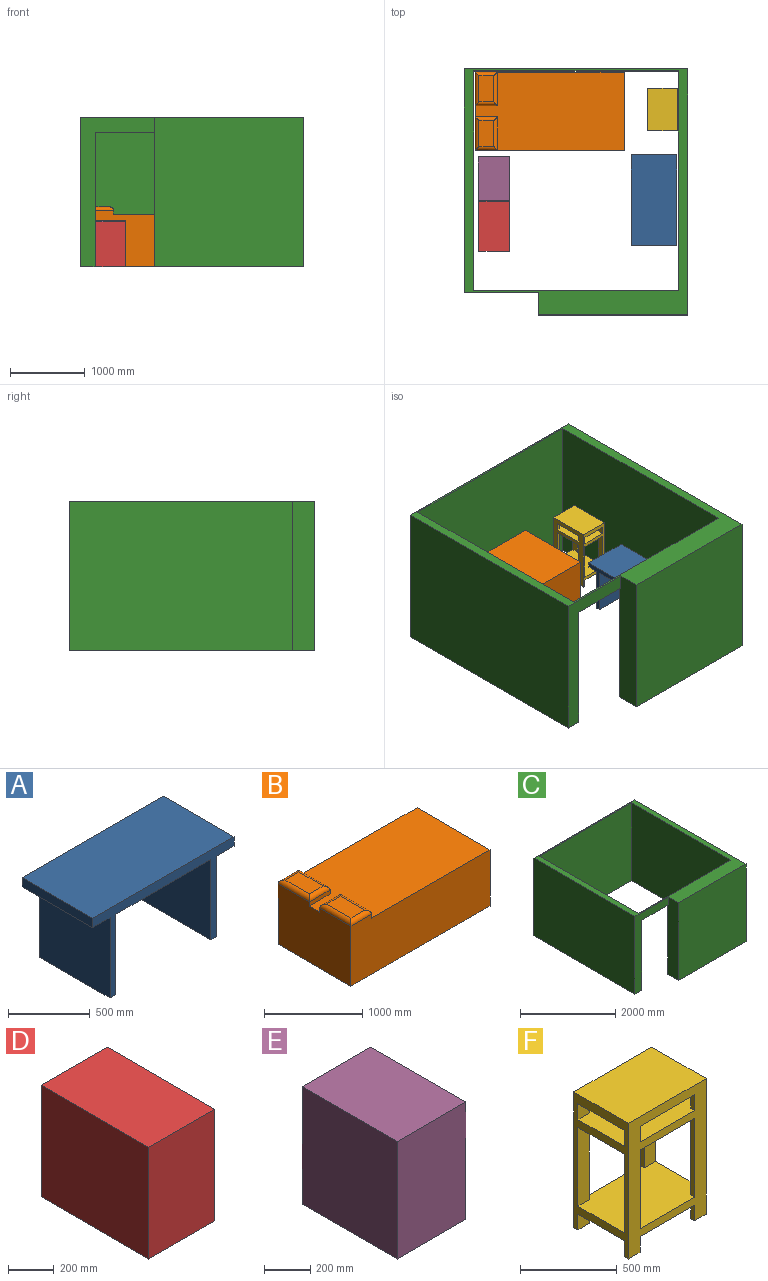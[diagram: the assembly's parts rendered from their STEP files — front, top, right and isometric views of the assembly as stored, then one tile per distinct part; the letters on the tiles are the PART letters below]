
ASSEMBLY  parts=6 mates=6
PART A: 14 faces, bbox 1220x610x670 mm
  f0: plane 610x50mm, normal (0,0,-1), area 30500mm2, adj f2,f3,f8,f13
  f1: plane 610x50mm, normal (0,0,-1), area 30500mm2, adj f2,f3,f9,f11
  f2: plane 1220x670mm, normal (0,-1,0), area 145400mm2, adj f0,f1,f4,f5,f6,f7,f8,f9
  f3: plane 1220x670mm, normal (0,1,0), area 145400mm2, adj f0,f1,f4,f5,f6,f7,f8,f9
  f4: plane 610x70mm, normal (-1,0,0), area 42700mm2, adj f2,f3,f6,f12
  f5: plane 610x70mm, normal (1,0,0), area 42700mm2, adj f2,f3,f6,f10
  f6: plane 1220x610mm, normal (0,0,1), area 744200mm2, adj f2,f3,f4,f5
  f7: plane 820x610mm, normal (0,0,-1), area 500200mm2, adj f2,f3,f8,f9
  f8: plane 610x600mm, normal (1,0,0), area 366000mm2, adj f0,f2,f3,f7
  f9: plane 610x600mm, normal (-1,0,0), area 366000mm2, adj f1,f2,f3,f7
  f10: plane 610x150mm, normal (0,0,-1), area 91500mm2, adj f2,f3,f5,f11
  f11: plane 610x600mm, normal (1,0,0), area 366000mm2, adj f1,f2,f3,f10
  f12: plane 610x150mm, normal (0,0,-1), area 91500mm2, adj f2,f3,f4,f13
  f13: plane 610x600mm, normal (-1,0,0), area 366000mm2, adj f0,f2,f3,f12
PART B: 20 faces, bbox 2000x1050x800 mm
  f0: plane 2000x1050mm, normal (0,0,1), area 1830000mm2, adj f1,f2,f3,f4,f6,f7,f9,f10
  f1: plane 2000x750mm, normal (0,1,0), area 1415000mm2, adj f0,f2,f4,f5,f7,f17
  f2: plane 1050x750mm, normal (-1,0,0), area 780000mm2, adj f0,f1,f3,f5,f6,f9,f13,f16
  f3: plane 2000x750mm, normal (0,-1,0), area 1415000mm2, adj f0,f2,f4,f5,f10,f15
  f4: plane 1050x700mm, normal (1,0,0), area 735000mm2, adj f0,f1,f3,f5
  f5: plane 2000x1050mm, normal (0,0,-1), area 2100000mm2, adj f1,f2,f3,f4
  f6: plane 300x50mm, normal (0,-1,0), area 15000mm2, adj f0,f2,f7,f18
  f7: plane 450x50mm, normal (1,0,0), area 22500mm2, adj f0,f1,f6,f19
  f8: plane 350x200mm, normal (0,0,1), area 70000mm2, adj f16,f17,f18,f19
  f9: plane 300x50mm, normal (0,1,0), area 15000mm2, adj f0,f2,f10,f12
  f10: plane 450x50mm, normal (1,0,0), area 22500mm2, adj f0,f3,f9,f14
  f11: plane 350x200mm, normal (0,0,1), area 70000mm2, adj f12,f13,f14,f15
  f12: cylinder r=50mm len=300mm, axis (1,0,0), area 20708mm2, adj f9,f11,f13,f14
  f13: cylinder r=50mm len=450mm, axis (0,1,0), area 32488.9mm2, adj f2,f11,f12,f15
  f14: cylinder r=50mm len=450mm, axis (0,-1,0), area 32488.9mm2, adj f10,f11,f12,f15
  f15: cylinder r=50mm len=300mm, axis (-1,0,0), area 20708mm2, adj f3,f11,f13,f14
  f16: cylinder r=50mm len=450mm, axis (0,1,0), area 32488.9mm2, adj f2,f8,f17,f18
  f17: cylinder r=50mm len=300mm, axis (1,0,0), area 20708mm2, adj f1,f8,f16,f19
  f18: cylinder r=50mm len=300mm, axis (-1,0,0), area 20708mm2, adj f6,f8,f16,f19
  f19: cylinder r=50mm len=450mm, axis (0,-1,0), area 32488.9mm2, adj f7,f8,f17,f18
PART C: 14 faces, bbox 3000x3300x2000 mm
  f0: plane 2000x1000mm, normal (0,-1,0), area 560000mm2, adj f2,f8,f9,f10,f12,f13
  f1: plane 3000x2000mm, normal (0,1,0), area 6000000mm2, adj f2,f7,f8,f9
  f2: plane 3000x2000mm, normal (-1,0,0), area 6000000mm2, adj f0,f1,f8,f9
  f3: plane 2950x2000mm, normal (1,0,0), area 5900000mm2, adj f4,f6,f8,f9
  f4: plane 2750x2000mm, normal (0,-1,0), area 5500000mm2, adj f3,f5,f8,f9
  f5: plane 2950x2000mm, normal (-1,0,0), area 5900000mm2, adj f4,f6,f8,f9
  f6: plane 2750x2000mm, normal (0,1,0), area 4060000mm2, adj f3,f5,f8,f9,f10,f12,f13
  f7: plane 3300x2000mm, normal (1,0,0), area 6600000mm2, adj f1,f8,f9,f11
  f8: plane 3300x3000mm, normal (0,0,1), area 1487500mm2, adj f0,f1,f2,f3,f4,f5,f6,f7
  f9: plane 3300x3000mm, normal (0,0,-1), area 1467500mm2, adj f0,f1,f2,f3,f4,f5,f6,f7
  f10: plane 2000x325mm, normal (-1,0,0), area 645000mm2, adj f0,f6,f8,f9,f11,f12
  f11: plane 2000x2000mm, normal (0,-1,0), area 4000000mm2, adj f7,f8,f9,f10
  f12: plane 800x25mm, normal (0,0,-1), area 20000mm2, adj f0,f6,f10,f13
  f13: plane 1800x25mm, normal (1,0,0), area 45000mm2, adj f0,f6,f9,f12
PART D: 6 faces, bbox 410x670x600 mm
  f0: plane 670x600mm, normal (-1,0,0), area 402000mm2, adj f1,f3,f4,f5
  f1: plane 600x410mm, normal (0,-1,0), area 246000mm2, adj f0,f2,f4,f5
  f2: plane 670x600mm, normal (1,0,0), area 402000mm2, adj f1,f3,f4,f5
  f3: plane 600x410mm, normal (0,1,0), area 246000mm2, adj f0,f2,f4,f5
  f4: plane 670x410mm, normal (0,0,1), area 274700mm2, adj f0,f1,f2,f3
  f5: plane 670x410mm, normal (0,0,-1), area 274700mm2, adj f0,f1,f2,f3
PART E: 6 faces, bbox 420x580x620 mm
  f0: plane 620x580mm, normal (-1,0,0), area 359600mm2, adj f1,f3,f4,f5
  f1: plane 620x420mm, normal (0,-1,0), area 260400mm2, adj f0,f2,f4,f5
  f2: plane 620x580mm, normal (1,0,0), area 359600mm2, adj f1,f3,f4,f5
  f3: plane 620x420mm, normal (0,1,0), area 260400mm2, adj f0,f2,f4,f5
  f4: plane 580x420mm, normal (0,0,1), area 243600mm2, adj f0,f1,f2,f3
  f5: plane 580x420mm, normal (0,0,-1), area 243600mm2, adj f0,f1,f2,f3
PART F: 38 faces, bbox 570x400x860 mm
  f0: plane 85x30mm, normal (0,0,-1), area 2550mm2, adj f3,f5,f12,f34
  f1: plane 85x30mm, normal (0,0,-1), area 2550mm2, adj f2,f4,f12,f37
  f2: plane 860x400mm, normal (-1,0,0), area 106000mm2, adj f1,f11,f12,f13,f14,f15,f18,f20
  f3: plane 860x400mm, normal (1,0,0), area 106000mm2, adj f0,f10,f11,f12,f13,f15,f18,f20
  f4: plane 100x30mm, normal (1,0,0), area 3000mm2, adj f1,f12,f15,f37
  f5: plane 100x30mm, normal (-1,0,0), area 3000mm2, adj f0,f12,f15,f34
  f6: plane 500x30mm, normal (1,0,0), area 15000mm2, adj f12,f18,f20,f33
  f7: plane 500x30mm, normal (-1,0,0), area 15000mm2, adj f12,f18,f20,f30
  f8: plane 100x30mm, normal (1,0,0), area 3000mm2, adj f12,f22,f24,f29
  f9: plane 100x30mm, normal (-1,0,0), area 3000mm2, adj f12,f22,f24,f26
  f10: plane 85x30mm, normal (0,0,-1), area 2550mm2, adj f3,f11,f17,f35
  f11: plane 860x570mm, normal (0,1,0), area 210200mm2, adj f2,f3,f10,f13,f14,f15,f16,f17
  f12: plane 860x570mm, normal (0,-1,0), area 210200mm2, adj f0,f1,f2,f3,f4,f5,f6,f7
  f13: plane 570x400mm, normal (0,0,1), area 228000mm2, adj f2,f3,f11,f12
  f14: plane 85x30mm, normal (0,0,-1), area 2550mm2, adj f2,f11,f16,f36
  f15: plane 570x400mm, normal (0,0,-1), area 217800mm2, adj f2,f3,f4,f5,f11,f12,f16,f17
  f16: plane 100x30mm, normal (1,0,0), area 3000mm2, adj f11,f14,f15,f36
  f17: plane 100x30mm, normal (-1,0,0), area 3000mm2, adj f10,f11,f15,f35
  f18: plane 570x400mm, normal (0,0,-1), area 217800mm2, adj f2,f3,f6,f7,f11,f12,f19,f21
  f19: plane 500x30mm, normal (1,0,0), area 15000mm2, adj f11,f18,f20,f32
  f20: plane 570x400mm, normal (0,0,1), area 217800mm2, adj f2,f3,f6,f7,f11,f12,f19,f21
  f21: plane 500x30mm, normal (-1,0,0), area 15000mm2, adj f11,f18,f20,f31
  f22: plane 570x400mm, normal (0,0,-1), area 217800mm2, adj f2,f3,f8,f9,f11,f12,f23,f25
  f23: plane 100x30mm, normal (1,0,0), area 3000mm2, adj f11,f22,f24,f28
  f24: plane 570x400mm, normal (0,0,1), area 217800mm2, adj f2,f3,f8,f9,f11,f12,f23,f25
  f25: plane 100x30mm, normal (-1,0,0), area 3000mm2, adj f11,f22,f24,f27
  f26: plane 100x85mm, normal (0,1,0), area 8500mm2, adj f3,f9,f22,f24
  f27: plane 100x85mm, normal (0,-1,0), area 8500mm2, adj f3,f22,f24,f25
  f28: plane 100x85mm, normal (0,-1,0), area 8500mm2, adj f2,f22,f23,f24
  f29: plane 100x85mm, normal (0,1,0), area 8500mm2, adj f2,f8,f22,f24
  f30: plane 500x85mm, normal (0,1,0), area 42500mm2, adj f3,f7,f18,f20
  f31: plane 500x85mm, normal (0,-1,0), area 42500mm2, adj f3,f18,f20,f21
  f32: plane 500x85mm, normal (0,-1,0), area 42500mm2, adj f2,f18,f19,f20
  f33: plane 500x85mm, normal (0,1,0), area 42500mm2, adj f2,f6,f18,f20
  f34: plane 100x85mm, normal (0,1,0), area 8500mm2, adj f0,f3,f5,f15
  f35: plane 100x85mm, normal (0,-1,0), area 8500mm2, adj f3,f10,f15,f17
  f36: plane 100x85mm, normal (0,-1,0), area 8500mm2, adj f2,f14,f15,f16
  f37: plane 100x85mm, normal (0,1,0), area 8500mm2, adj f1,f2,f4,f15
PLACE A rot(axis=(0,0,-1),90deg) t=(1695.17,1536.24,-161.15)mm
PLACE B t=(-402.6,1596.34,-161.15)mm
PLACE C t=(-548.42,-312.78,-161.15)mm
PLACE D t=(-351.72,242.88,-161.15)mm
PLACE E t=(-361.72,927.88,-161.15)mm
PLACE F rot(axis=(0,0,-1),90deg) t=(1912.29,2428.6,-161.15)mm
MATE planar C.f9 <-> A.f1  axis (0,0,-1) through (1168.28,532.88,-161.15)mm
MATE planar E.f2 <-> D.f2  axis (1,0,0) through (58.28,1217.88,148.85)mm
MATE planar F.f0 <-> C.f9  axis (0,0,-1) through (1927.29,1901.1,-161.15)mm
MATE planar D.f5 <-> C.f9  axis (0,0,-1) through (-146.72,577.88,-161.15)mm
MATE planar E.f5 <-> C.f9  axis (0,0,-1) through (-151.72,1217.88,-161.15)mm
MATE planar C.f9 <-> B.f5  axis (0,0,-1) through (1389.08,-287.78,-161.15)mm
